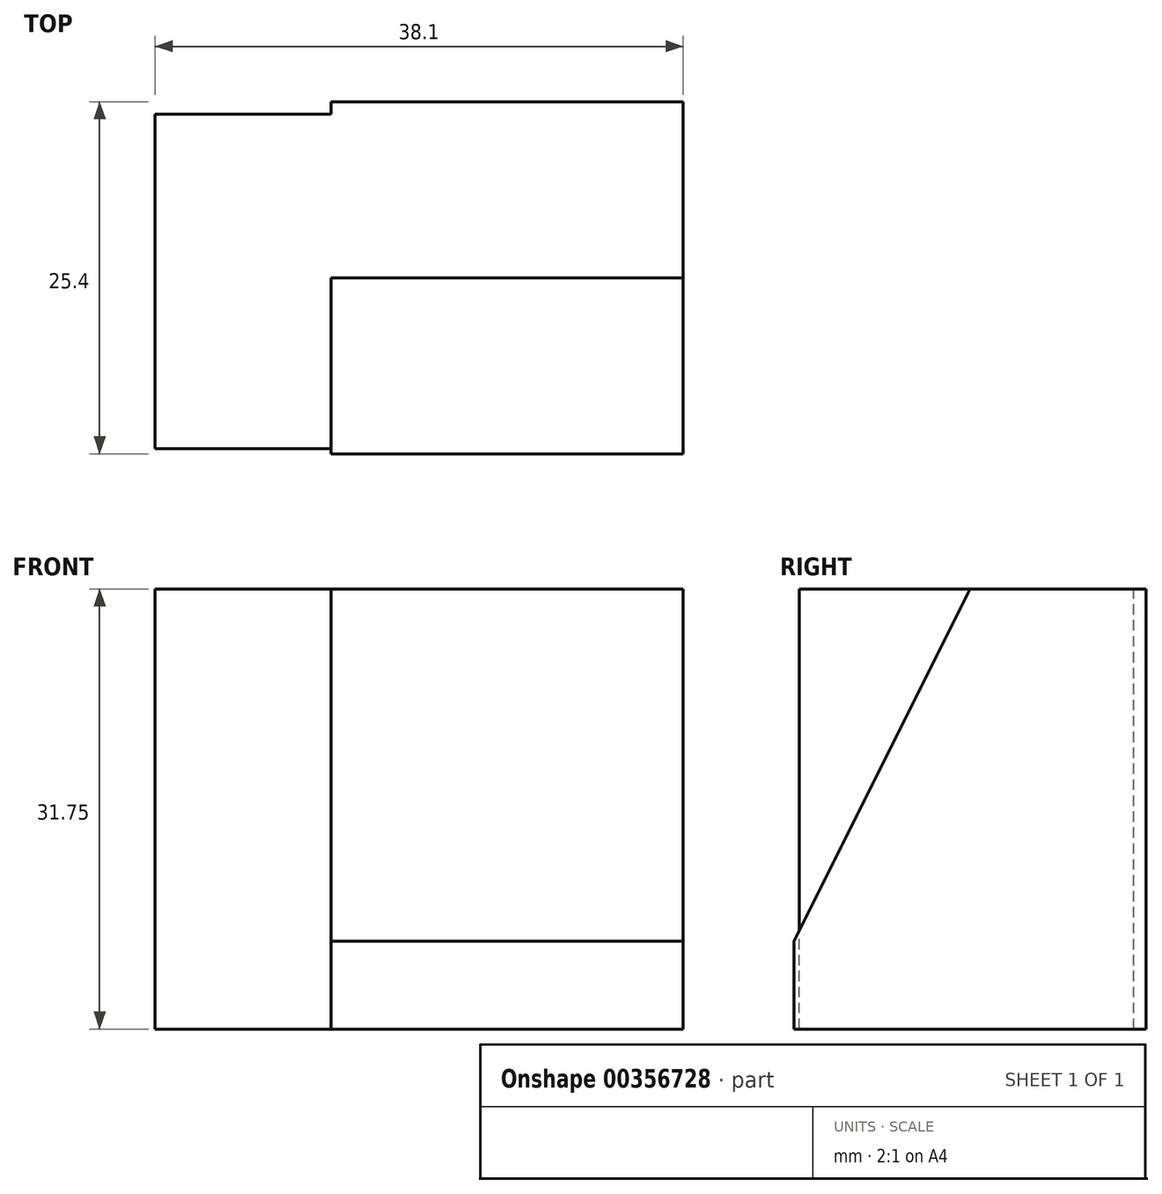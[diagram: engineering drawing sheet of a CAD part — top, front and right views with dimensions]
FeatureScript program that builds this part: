
annotation { "Feature Type Name" : "Feature", "Feature Type Description" : "" }
export const myFeature = defineFeature(function(context is Context, id is Id, definition is map)
    precondition{}
    {
        {
            var Q0;
            Q0=qCreatedBy(makeId("Right.planeOp"),FACE);
            var sketch = newSketch(context, id + "F0", { "sketchPlane" : qUnion([Q0])});
            skLineSegment(sketch, "E0", {"start": v(46.62, 0) * mm, "end": v(46.62, 31.75) * mm});
            skLineSegment(sketch, "E1", {"start": v(46.62, 31.75) * mm, "end": v(33.92, 31.75) * mm});
            skLineSegment(sketch, "E2", {"start": v(21.22, 0) * mm, "end": v(46.62, 0) * mm});
            skLineSegment(sketch, "E3", {"start": v(21.22, 0) * mm, "end": v(21.22, 6.35) * mm});
            skLineSegment(sketch, "E4", {"start": v(21.22, 6.35) * mm, "end": v(33.92, 31.75) * mm});
            skSolve(sketch);
        }
        {
            var Q0;
            Q0=makeQuery(id+"F0.imprint","IMPRINT",FACE,{"disambiguationData":[TD([[makeQuery(id+"F0.imprint","IMPRINT",EDGE,{"derivedFrom":sQuery(id+"F0.wireOp",EDGE,"E0")}),1.0]])]});
            extrude(context, id + "F1", {"entities" : qUnion([Q0]), "depth" : 25.4 * mm});
        }
        {
            var Q0;
            Q0=qCreatedBy(makeId("Right.planeOp"),FACE);
            var sketch = newSketch(context, id + "F2", { "sketchPlane" : qUnion([Q0])});
            skLineSegment(sketch, "E5", {"start": v(45.72, 0) * mm, "end": v(45.72, 31.75) * mm});
            skLineSegment(sketch, "E6", {"start": v(45.72, 31.75) * mm, "end": v(20.32, 31.75) * mm});
            skLineSegment(sketch, "E7", {"start": v(21.6, 0) * mm, "end": v(21.6, 31.75) * mm});
            skLineSegment(sketch, "E8", {"start": v(21.6, 0) * mm, "end": v(45.72, 0) * mm});
            skSolve(sketch);
        }
        {
            var Q0;
            {var subQ0=sQuery(id+"F2.wireOp",EDGE,"E5");Q0=makeQuery(id+"F2.imprint","IMPRINT",FACE,{"disambiguationData":[TD([[makeQuery(id+"F2.imprint","IMPRINT",EDGE,{"derivedFrom":subQ0}),1.0]])]});}
            extrude(context, id + "F3", {"entities" : qUnion([Q0]), "operationType" : NewBodyOperationType.ADD, "oppositeDirection" : true, "depth" : 12.7 * mm});
        }
    });
